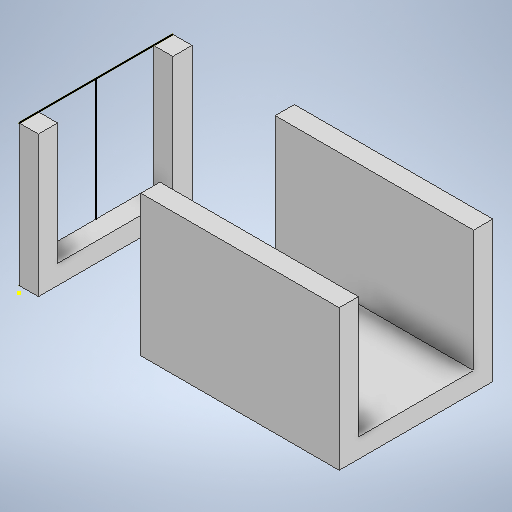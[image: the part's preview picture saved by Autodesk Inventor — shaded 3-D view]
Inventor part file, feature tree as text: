
AUTODESK INVENTOR PART (.ipt)
format: ipt  version: 2025.1 (Build 291241020, 241B)  size: 308,224 bytes
history: native  units: in
note: dims shown in document units (in); Inventor stores cm internally (conversion verified against a paired STEP export)
features: sketch x10, extrude x9
ambient origin geometry x8: Origin, YZ Plane, XZ Plane, XY Plane, X Axis, Y Axis, Z Axis, Center Point
bodies: Body1 (feature_tree)
feature tree (19):
  extrude  "Extrusion2"  Depth=0.9449in
  extrude  "Extrusion3"  Depth=1.378in
  extrude  "Extrusion4"  Depth=0.7087in TaperAngle=0.0deg
  extrude  "Extrusion5"  Depth=0.0394in TaperAngle=0.0deg
  sketch  "Sketch7"  dims[d18=0.5906in d19=0.0in d20=0.1181in]
  extrude  "Extrusion6"  Depth=0.1181in
  extrude  "Extrusion7"  Depth=0.7087in
  extrude  "Extrusion8"  Depth=0.1181in
  extrude  "Extrusion10"  Depth=0.6299in
  extrude  "Extrusion11"  Depth=0.2362in
  sketch  "Sketch3"  dims[d7=1.378in d8=0.9449in]
  sketch  "Sketch4"  dims[d9=0.9055in d10=0.0in d11=1.378in]
  sketch  "Sketch5"  dims[d12=0.7087in d13=0.7874in d14=0.0in]
  sketch  "Sketch6"  dims[d15=0.0394in d16=1.9749in d17=0.0in]
  sketch  "Sketch8"  dims[d21=0.5906in d22=0.0in d23=0.7087in]
  sketch  "Sketch9"  dims[d24=0.3937in d25=0.0in d26=0.1181in]
  sketch  "Sketch10"  dims[d27=0.6299in d28=0.4921in]
  sketch  "Sketch12"  dims[d29=1.2062in d30=0.0in d34=0.2362in]
  sketch  "Sketch13"  dims[d35=0.315in d36=0.0787in d37=0.0787in d38=0.3937in d39=0.0in d40=0.6299in d41=0.3937in d42=0.0in]
